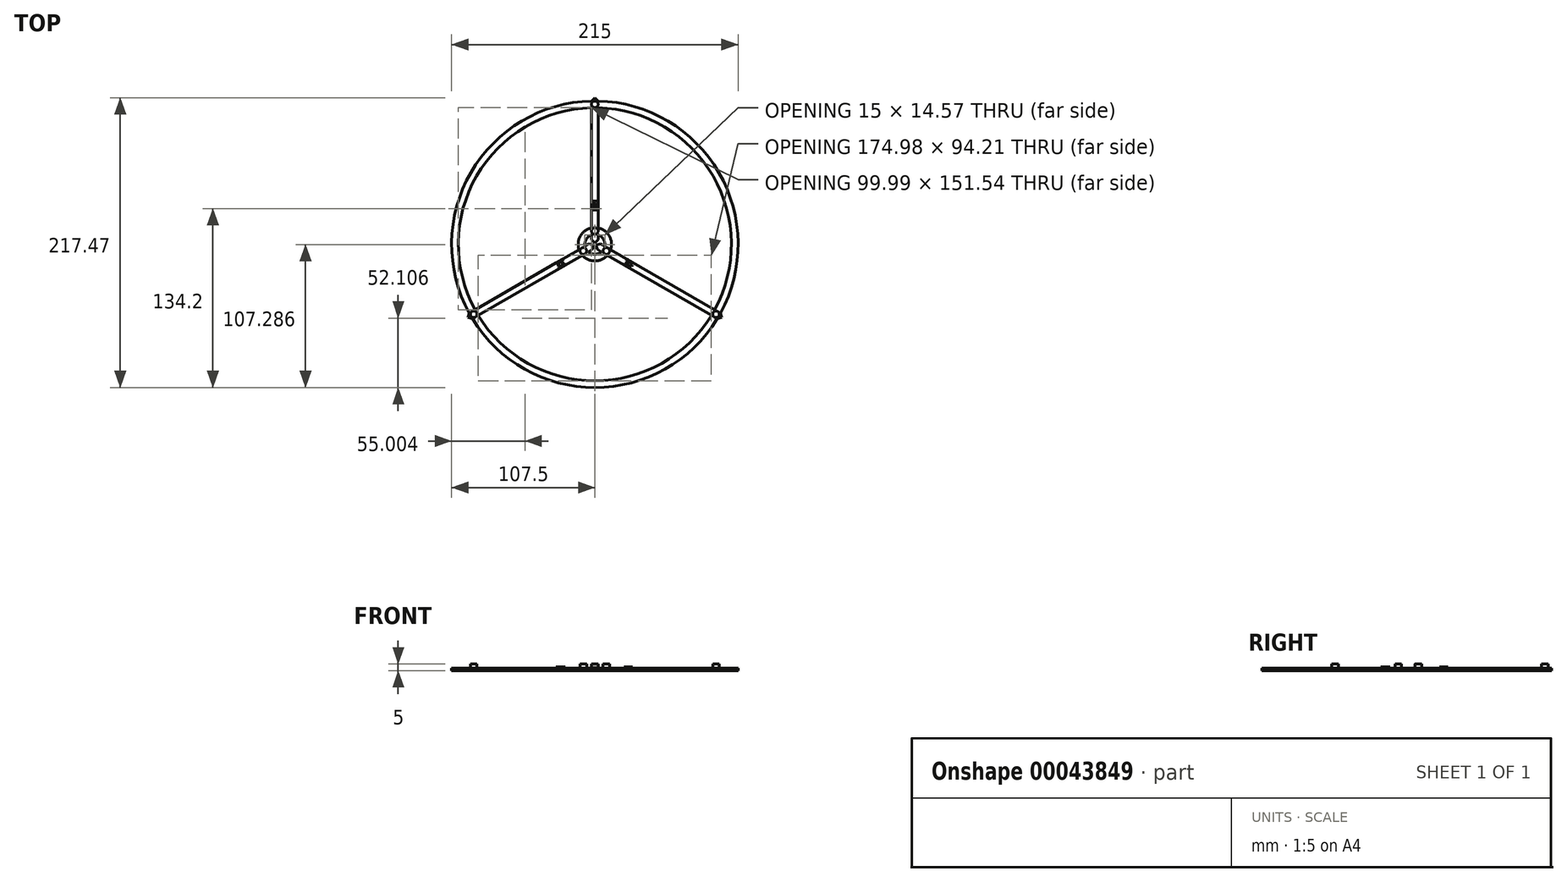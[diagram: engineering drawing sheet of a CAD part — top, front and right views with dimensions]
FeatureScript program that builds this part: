
annotation { "Feature Type Name" : "Feature", "Feature Type Description" : "" }
export const myFeature = defineFeature(function(context is Context, id is Id, definition is map)
    precondition{}
    {
        {
            var Q0;
            Q0=qCreatedBy(makeId("Top.planeOp"),FACE);
            var sketch = newSketch(context, id + "F0", { "sketchPlane" : qUnion([Q0])});
            skLineSegment(sketch, "E0", {"start": v(0, 0) * mm, "end": v(0, 109.97) * mm, "construction": true});
            skLineSegment(sketch, "E1", {"start": v(0, 109.97) * mm, "end": v(-2.5, 107.47) * mm});
            skLineSegment(sketch, "E2", {"start": v(-2.5, 102.47) * mm, "end": v(-2.5, 12.25) * mm});
            skLineSegment(sketch, "E3", {"start": v(-2.5, 7.07) * mm, "end": v(-2.5, 3.5) * mm});
            skLineSegment(sketch, "E4", {"start": v(-2.5, 3.5) * mm, "end": v(0, 1) * mm});
            skLineSegment(sketch, "E5.MirrorCS", {"start": v(2.5, 3.5) * mm, "end": v(0, 1) * mm});
            skLineSegment(sketch, "E6.MirrorCS", {"start": v(2.5, 7.07) * mm, "end": v(2.5, 3.5) * mm});
            skLineSegment(sketch, "E7.MirrorCS", {"start": v(0, 109.97) * mm, "end": v(2.5, 107.47) * mm});
            skLineSegment(sketch, "E8.MirrorCS", {"start": v(2.5, 102.47) * mm, "end": v(2.5, 12.25) * mm});
            skLineSegment(sketch, "E9.1.0", {"start": v(-1.78, -3.92) * mm, "end": v(-0.87, -0.5) * mm});
            skLineSegment(sketch, "E9.1.1", {"start": v(-4.28, 0.42) * mm, "end": v(-0.87, -0.5) * mm});
            skLineSegment(sketch, "E9.1.2", {"start": v(-7.37, -1.37) * mm, "end": v(-4.28, 0.42) * mm});
            skLineSegment(sketch, "E9.1.3", {"start": v(-4.87, -5.7) * mm, "end": v(-1.78, -3.92) * mm});
            skLineSegment(sketch, "E9.1.4", {"start": v(-87.5, -53.4) * mm, "end": v(-9.36, -8.29) * mm});
            skLineSegment(sketch, "E9.1.5", {"start": v(-90, -49.07) * mm, "end": v(-11.86, -3.96) * mm});
            skLineSegment(sketch, "E9.1.6", {"start": v(-95.24, -54.99) * mm, "end": v(-94.32, -51.57) * mm});
            skLineSegment(sketch, "E9.1.7", {"start": v(-95.24, -54.99) * mm, "end": v(-91.82, -55.9) * mm});
            skLineSegment(sketch, "E9.2.0", {"start": v(4.28, 0.42) * mm, "end": v(0.87, -0.5) * mm});
            skLineSegment(sketch, "E9.2.1", {"start": v(1.78, -3.92) * mm, "end": v(0.87, -0.5) * mm});
            skLineSegment(sketch, "E9.2.2", {"start": v(4.87, -5.7) * mm, "end": v(1.78, -3.92) * mm});
            skLineSegment(sketch, "E9.2.3", {"start": v(7.37, -1.37) * mm, "end": v(4.28, 0.42) * mm});
            skLineSegment(sketch, "E9.2.4", {"start": v(90, -49.07) * mm, "end": v(11.86, -3.96) * mm});
            skLineSegment(sketch, "E9.2.5", {"start": v(87.5, -53.4) * mm, "end": v(9.36, -8.29) * mm});
            skLineSegment(sketch, "E9.2.6", {"start": v(95.24, -54.99) * mm, "end": v(91.82, -55.9) * mm});
            skLineSegment(sketch, "E9.2.7", {"start": v(95.24, -54.99) * mm, "end": v(94.32, -51.57) * mm});
            skPoint(sketch, "E9.center", {"position": v(0, 0) * mm});
            skCircle(sketch, "E10", {"center": v(0, 105) * mm, "radius": 2.5 * mm});
            skCircle(sketch, "E11.1.0", {"center": v(-90.93, -52.5) * mm, "radius": 2.5 * mm});
            skCircle(sketch, "E11.2.0", {"center": v(90.93, -52.5) * mm, "radius": 2.5 * mm});
            skArc(sketch, "E12", {"start": v(-11.86, -3.96) * mm, "mid": v(-10.83, -6.25) * mm, "end": v(-9.36, -8.29) * mm, "construction": true});
            skArc(sketch, "E13", {"start": v(-9.36, -8.29) * mm, "mid": v(0, -12.5) * mm, "end": v(9.36, -8.29) * mm});
            skArc(sketch, "E14", {"start": v(9.36, -8.29) * mm, "mid": v(10.83, -6.25) * mm, "end": v(11.86, -3.96) * mm, "construction": true});
            skArc(sketch, "E15", {"start": v(11.86, -3.96) * mm, "mid": v(10.83, 6.25) * mm, "end": v(2.5, 12.25) * mm});
            skArc(sketch, "E16", {"start": v(2.5, 12.25) * mm, "mid": v(0, 12.5) * mm, "end": v(-2.5, 12.25) * mm, "construction": true});
            skArc(sketch, "E17", {"start": v(-2.5, 12.25) * mm, "mid": v(-10.83, 6.25) * mm, "end": v(-11.86, -3.96) * mm});
            skArc(sketch, "E18", {"start": v(87.5, -53.4) * mm, "mid": v(88.77, -51.25) * mm, "end": v(90, -49.07) * mm, "construction": true});
            skArc(sketch, "E19", {"start": v(90, -49.07) * mm, "mid": v(88.77, 51.25) * mm, "end": v(2.5, 102.47) * mm});
            skArc(sketch, "E20", {"start": v(94.32, -51.57) * mm, "mid": v(93.1, 53.75) * mm, "end": v(2.5, 107.47) * mm});
            skArc(sketch, "E21", {"start": v(91.82, -55.9) * mm, "mid": v(93.1, -53.75) * mm, "end": v(94.32, -51.57) * mm, "construction": true});
            skArc(sketch, "E22", {"start": v(-91.82, -55.9) * mm, "mid": v(0, -107.5) * mm, "end": v(91.82, -55.9) * mm});
            skArc(sketch, "E23", {"start": v(-94.32, -51.57) * mm, "mid": v(-93.1, -53.75) * mm, "end": v(-91.82, -55.9) * mm, "construction": true});
            skArc(sketch, "E24", {"start": v(2.5, 107.47) * mm, "mid": v(0, 107.5) * mm, "end": v(-2.5, 107.47) * mm, "construction": true});
            skArc(sketch, "E25", {"start": v(-2.5, 107.47) * mm, "mid": v(-93.1, 53.75) * mm, "end": v(-94.32, -51.57) * mm});
            skArc(sketch, "E26", {"start": v(-2.5, 102.47) * mm, "mid": v(-88.77, 51.25) * mm, "end": v(-90, -49.07) * mm});
            skArc(sketch, "E27", {"start": v(2.5, 102.47) * mm, "mid": v(0, 102.5) * mm, "end": v(-2.5, 102.47) * mm, "construction": true});
            skArc(sketch, "E28", {"start": v(-90, -49.07) * mm, "mid": v(-88.77, -51.25) * mm, "end": v(-87.5, -53.4) * mm, "construction": true});
            skArc(sketch, "E29", {"start": v(-87.5, -53.4) * mm, "mid": v(0, -102.5) * mm, "end": v(87.5, -53.4) * mm});
            skArc(sketch, "E30", {"start": v(-2.5, 7.07) * mm, "mid": v(-6.5, 3.75) * mm, "end": v(-7.37, -1.37) * mm});
            skArc(sketch, "E31", {"start": v(2.5, 7.07) * mm, "mid": v(0, 7.5) * mm, "end": v(-2.5, 7.07) * mm, "construction": true});
            skArc(sketch, "E32", {"start": v(7.37, -1.37) * mm, "mid": v(6.5, 3.75) * mm, "end": v(2.5, 7.07) * mm});
            skArc(sketch, "E33", {"start": v(4.87, -5.7) * mm, "mid": v(6.5, -3.75) * mm, "end": v(7.37, -1.37) * mm, "construction": true});
            skArc(sketch, "E34", {"start": v(-4.87, -5.7) * mm, "mid": v(0, -7.5) * mm, "end": v(4.87, -5.7) * mm});
            skArc(sketch, "E35", {"start": v(-7.37, -1.37) * mm, "mid": v(-6.5, -3.75) * mm, "end": v(-4.87, -5.7) * mm, "construction": true});
            skLineSegment(sketch, "E36", {"start": v(-11.86, -3.96) * mm, "end": v(-11.86, -3.96) * mm});
            skCircle(sketch, "E37", {"center": v(0, 10) * mm, "radius": 2.5 * mm});
            skCircle(sketch, "E38.1.0", {"center": v(-8.66, -5) * mm, "radius": 2.5 * mm});
            skCircle(sketch, "E38.2.0", {"center": v(8.66, -5) * mm, "radius": 2.5 * mm});
            skSolve(sketch);
        }
        {
            var Q0;
            Q0=makeQuery(id+"F0.imprint","IMPRINT",FACE,{"disambiguationData":[TD([[makeQuery(id+"F0.imprint","IMPRINT",EDGE,{"derivedFrom":sQuery(id+"F0.wireOp",EDGE,"E1")}),1.0]])]});
            extrude(context, id + "F1", {"entities" : qUnion([Q0]), "depth" : 2 * mm});
        }
        {
            var Q0;
            Q0=makeQuery(id+"F0.imprint","IMPRINT",FACE,{"disambiguationData":[TD([[makeQuery(id+"F0.imprint","IMPRINT",EDGE,{"derivedFrom":sQuery(id+"F0.wireOp",EDGE,"E11.1.0")}),1.0]])]});
            var Q1;
            Q1=makeQuery(id+"F0.imprint","IMPRINT",FACE,{"disambiguationData":[TD([[makeQuery(id+"F0.imprint","IMPRINT",EDGE,{"derivedFrom":sQuery(id+"F0.wireOp",EDGE,"E38.1.0")}),1.0]])]});
            var Q2;
            Q2=makeQuery(id+"F0.imprint","IMPRINT",FACE,{"disambiguationData":[TD([[makeQuery(id+"F0.imprint","IMPRINT",EDGE,{"derivedFrom":sQuery(id+"F0.wireOp",EDGE,"E38.2.0")}),1.0]])]});
            var Q3;
            Q3=makeQuery(id+"F0.imprint","IMPRINT",FACE,{"disambiguationData":[TD([[makeQuery(id+"F0.imprint","IMPRINT",EDGE,{"derivedFrom":sQuery(id+"F0.wireOp",EDGE,"E11.2.0")}),1.0]])]});
            var Q4;
            Q4=makeQuery(id+"F0.imprint","IMPRINT",FACE,{"disambiguationData":[TD([[makeQuery(id+"F0.imprint","IMPRINT",EDGE,{"derivedFrom":sQuery(id+"F0.wireOp",EDGE,"E37")}),1.0]])]});
            var Q5;
            Q5=makeQuery(id+"F0.imprint","IMPRINT",FACE,{"disambiguationData":[TD([[makeQuery(id+"F0.imprint","IMPRINT",EDGE,{"derivedFrom":sQuery(id+"F0.wireOp",EDGE,"E10")}),1.0]])]});
            extrude(context, id + "F2", {"entities" : qUnion([Q0, Q1, Q2, Q3, Q4, Q5]), "operationType" : NewBodyOperationType.ADD, "flatOperationType" : FlatOperationType.REMOVE, "offsetDistance" : 25 * mm, "depth" : 5 * mm, "domain" : OperationDomain.MODEL});
        }
        {
            var Q0;
            Q0=makeQuery(id+"F1.opExtrude","CAP_FACE",FACE,{"disambiguationData":[OSD([sQuery(id+"F0.wireOp",EDGE,"E1"),sQuery(id+"F0.wireOp",EDGE,"E2"),sQuery(id+"F0.wireOp",EDGE,"E3"),sQuery(id+"F0.wireOp",EDGE,"E4"),sQuery(id+"F0.wireOp",EDGE,"E5.MirrorCS"),sQuery(id+"F0.wireOp",EDGE,"E6.MirrorCS"),sQuery(id+"F0.wireOp",EDGE,"E7.MirrorCS"),sQuery(id+"F0.wireOp",EDGE,"E8.MirrorCS"),sQuery(id+"F0.wireOp",EDGE,"E9.1.0"),sQuery(id+"F0.wireOp",EDGE,"E9.1.1"),sQuery(id+"F0.wireOp",EDGE,"E9.1.2"),sQuery(id+"F0.wireOp",EDGE,"E9.1.3"),sQuery(id+"F0.wireOp",EDGE,"E9.1.4"),sQuery(id+"F0.wireOp",EDGE,"E9.1.5"),sQuery(id+"F0.wireOp",EDGE,"E9.1.6"),sQuery(id+"F0.wireOp",EDGE,"E9.1.7"),sQuery(id+"F0.wireOp",EDGE,"E9.2.0"),sQuery(id+"F0.wireOp",EDGE,"E9.2.1"),sQuery(id+"F0.wireOp",EDGE,"E9.2.2"),sQuery(id+"F0.wireOp",EDGE,"E9.2.3"),sQuery(id+"F0.wireOp",EDGE,"E9.2.4"),sQuery(id+"F0.wireOp",EDGE,"E9.2.5"),sQuery(id+"F0.wireOp",EDGE,"E9.2.6"),sQuery(id+"F0.wireOp",EDGE,"E9.2.7"),sQuery(id+"F0.wireOp",EDGE,"E10"),sQuery(id+"F0.wireOp",EDGE,"E11.1.0"),sQuery(id+"F0.wireOp",EDGE,"E11.2.0"),sQuery(id+"F0.wireOp",EDGE,"E13"),sQuery(id+"F0.wireOp",EDGE,"E15"),sQuery(id+"F0.wireOp",EDGE,"E17"),sQuery(id+"F0.wireOp",EDGE,"E19"),sQuery(id+"F0.wireOp",EDGE,"E20"),sQuery(id+"F0.wireOp",EDGE,"E22"),sQuery(id+"F0.wireOp",EDGE,"E25"),sQuery(id+"F0.wireOp",EDGE,"E26"),sQuery(id+"F0.wireOp",EDGE,"E29"),sQuery(id+"F0.wireOp",EDGE,"E30"),sQuery(id+"F0.wireOp",EDGE,"E32"),sQuery(id+"F0.wireOp",EDGE,"E34"),sQuery(id+"F0.wireOp",EDGE,"E37"),sQuery(id+"F0.wireOp",EDGE,"E38.1.0"),sQuery(id+"F0.wireOp",EDGE,"E38.2.0")])],"isStart":false});
            var sketch = newSketch(context, id + "F3", { "sketchPlane" : qUnion([Q0])});
            skText(sketch, "E39", { "text": "Z", "fontName": "OpenSans-Bold.ttf"});
            skText(sketch, "E40", { "text": "Y", "fontName": "OpenSans-Bold.ttf"});
            skPoint(sketch, "E41", {"position": v(48.42, -30.84) * mm});
            skText(sketch, "E42", { "text": "X", "fontName": "OpenSans-Bold.ttf"});
            skPoint(sketch, "E43", {"position": v(-50.92, -26.51) * mm});
            const initialGuessF3  = {"E39": [-0.0025, 0.02586, 1, 0, 0.00648], "E40": [0.02676, -0.01834, 0.5, 0.86603, 0.00577], "E42": [-0.02926, -0.014, 0.5, -0.86603, 0.0054]};
            skSetInitialGuess(sketch, initialGuessF3);
            skSolve(sketch);
        }
        {
            var Q0;
            Q0 = qSketchRegion(id + "F3", true);
            extrude(context, id + "F4", {"entities" : qUnion([Q0]), "operationType" : NewBodyOperationType.ADD, "depth" : 1 * mm});
        }
    });
